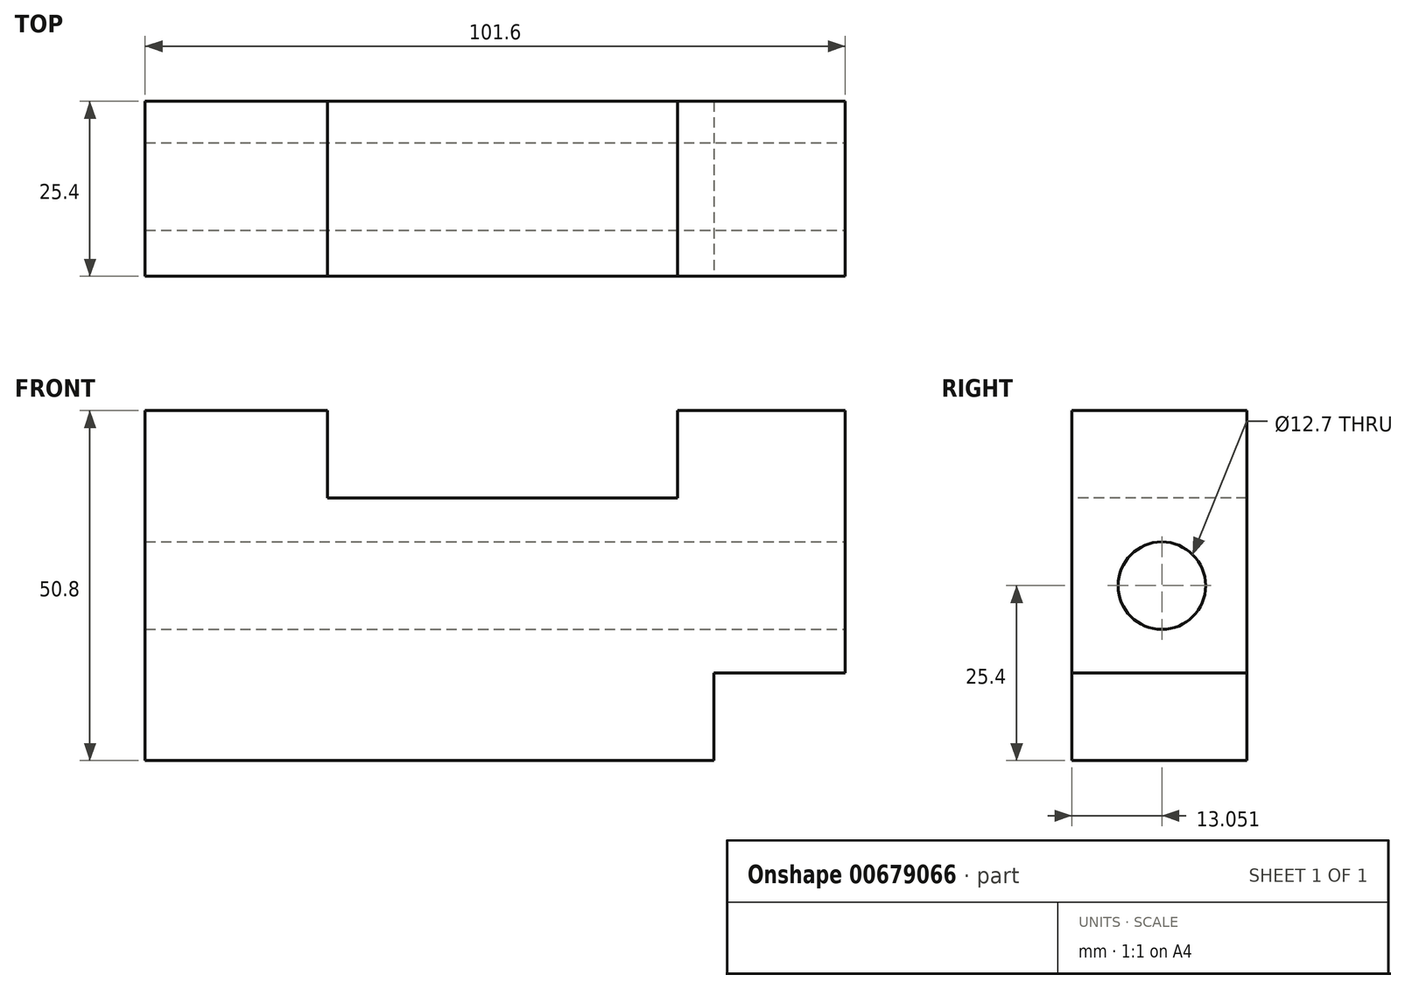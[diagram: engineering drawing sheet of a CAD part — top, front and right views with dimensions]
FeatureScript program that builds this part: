
annotation { "Feature Type Name" : "Feature", "Feature Type Description" : "" }
export const myFeature = defineFeature(function(context is Context, id is Id, definition is map)
    precondition{}
    {
        {
            var Q0;
            Q0=qCreatedBy(makeId("Front.planeOp"),FACE);
            var sketch = newSketch(context, id + "F0", { "sketchPlane" : qUnion([Q0])});
            skLineSegment(sketch, "E0.bottom", {"start": v(-50.8, 25.4) * mm, "end": v(50.8, 25.4) * mm});
            skLineSegment(sketch, "E0.top", {"start": v(-50.8, -25.4) * mm, "end": v(50.8, -25.4) * mm});
            skLineSegment(sketch, "E0.left", {"start": v(-50.8, 25.4) * mm, "end": v(-50.8, -25.4) * mm});
            skLineSegment(sketch, "E0.right", {"start": v(50.8, 25.4) * mm, "end": v(50.8, -25.4) * mm});
            skPoint(sketch, "E0.middle", {"position": v(0, 0) * mm});
            skSolve(sketch);
        }
        {
            var Q0;
            Q0 = qSketchRegion(id + "F0", true);
            extrude(context, id + "F1", {"entities" : qUnion([Q0]), "depth" : 25.4 * mm, "offsetDistance" : 25.4 * mm});
        }
        {
            var Q0;
            Q0=makeQuery(id+"F1.opExtrude","CAP_FACE",FACE,{"disambiguationData":[OSD([sQuery(id+"F0.wireOp",EDGE,"E0.bottom"),sQuery(id+"F0.wireOp",EDGE,"E0.top"),sQuery(id+"F0.wireOp",EDGE,"E0.left"),sQuery(id+"F0.wireOp",EDGE,"E0.right")])],"isStart":false});
            var sketch = newSketch(context, id + "F2", { "sketchPlane" : qUnion([Q0])});
            skLineSegment(sketch, "E1.bottom", {"start": v(-24.31, 25.4) * mm, "end": v(26.49, 25.4) * mm});
            skLineSegment(sketch, "E1.top", {"start": v(-24.31, 12.7) * mm, "end": v(26.49, 12.7) * mm});
            skLineSegment(sketch, "E1.left", {"start": v(-24.31, 25.4) * mm, "end": v(-24.31, 12.7) * mm});
            skLineSegment(sketch, "E1.right", {"start": v(26.49, 25.4) * mm, "end": v(26.49, 12.7) * mm});
            skSolve(sketch);
        }
        {
            var Q0;
            Q0=makeQuery(id+"F2.imprint","IMPRINT",FACE,{"disambiguationData":[TD([[makeQuery(id+"F2.imprint","IMPRINT",EDGE,{"derivedFrom":sQuery(id+"F2.wireOp",EDGE,"E1.bottom")}),-1.0]])]});
            extrude(context, id + "F3", {"entities" : qUnion([Q0]), "operationType" : NewBodyOperationType.REMOVE, "endBound" : BoundingType.THROUGH_ALL, "oppositeDirection" : true, "depth" : 25.4 * mm, "offsetDistance" : 25.4 * mm});
        }
        {
            var Q0;
            Q0=makeQuery(id+"F1.opExtrude","CAP_FACE",FACE,{"disambiguationData":[OSD([sQuery(id+"F0.wireOp",EDGE,"E0.bottom"),sQuery(id+"F0.wireOp",EDGE,"E0.top"),sQuery(id+"F0.wireOp",EDGE,"E0.left"),sQuery(id+"F0.wireOp",EDGE,"E0.right")])],"isStart":false});
            var sketch = newSketch(context, id + "F4", { "sketchPlane" : qUnion([Q0])});
            skLineSegment(sketch, "E2.bottom", {"start": v(50.8, -12.7) * mm, "end": v(31.75, -12.7) * mm});
            skLineSegment(sketch, "E2.top", {"start": v(50.8, -25.4) * mm, "end": v(31.75, -25.4) * mm});
            skLineSegment(sketch, "E2.left", {"start": v(50.8, -12.7) * mm, "end": v(50.8, -25.4) * mm});
            skLineSegment(sketch, "E2.right", {"start": v(31.75, -12.7) * mm, "end": v(31.75, -25.4) * mm});
            skSolve(sketch);
        }
        {
            var Q0;
            Q0=makeQuery(id+"F4.imprint","IMPRINT",FACE,{"disambiguationData":[TD([[makeQuery(id+"F4.imprint","IMPRINT",EDGE,{"derivedFrom":sQuery(id+"F4.wireOp",EDGE,"E2.bottom")}),1.0]])]});
            extrude(context, id + "F5", {"entities" : qUnion([Q0]), "operationType" : NewBodyOperationType.REMOVE, "endBound" : BoundingType.THROUGH_ALL, "oppositeDirection" : true, "depth" : 25.4 * mm, "offsetDistance" : 25.4 * mm});
        }
        {
            var Q0;
            Q0=makeQuery(id+"F1.opExtrude","SWEPT_FACE",FACE,{"disambiguationData":[OSD([sQuery(id+"F0.wireOp",EDGE,"E0.right")])]});
            var sketch = newSketch(context, id + "F6", { "sketchPlane" : qUnion([Q0])});
            skCircle(sketch, "E3", {"center": v(-12.35, 0) * mm, "radius": 6.35 * mm});
            skSolve(sketch);
        }
        {
            var Q0;
            Q0=makeQuery(id+"F6.imprint","IMPRINT",FACE,{"disambiguationData":[TD([[makeQuery(id+"F6.imprint","IMPRINT",EDGE,{"derivedFrom":sQuery(id+"F6.wireOp",EDGE,"E3")}),1.0]])]});
            extrude(context, id + "F7", {"entities" : qUnion([Q0]), "operationType" : NewBodyOperationType.REMOVE, "endBound" : BoundingType.THROUGH_ALL, "oppositeDirection" : true, "depth" : 25.4 * mm, "offsetDistance" : 25.4 * mm});
        }
    });
